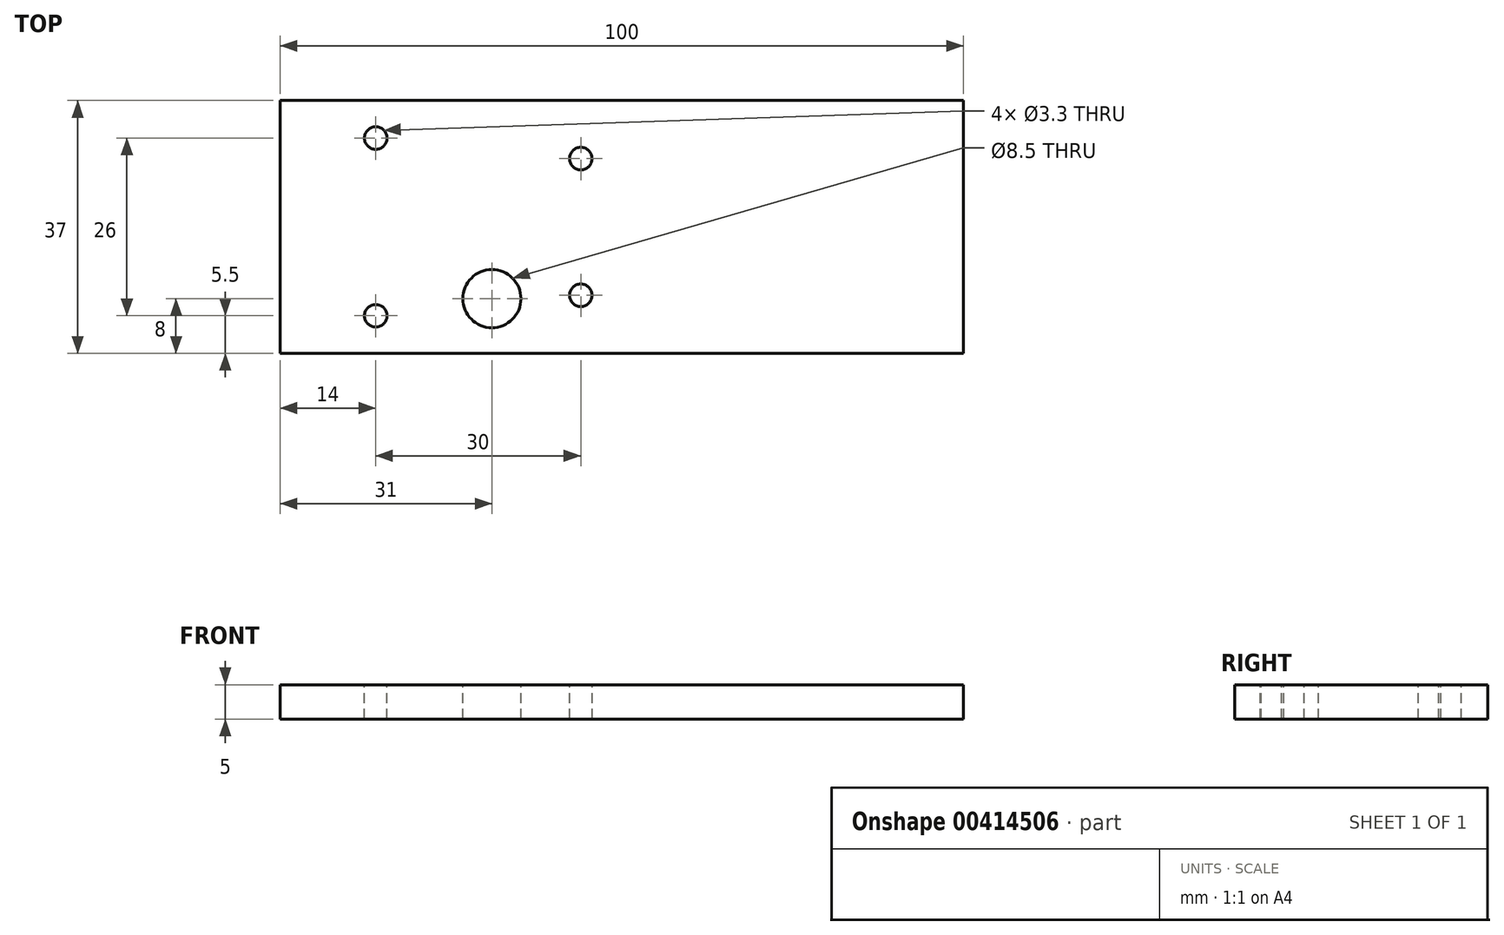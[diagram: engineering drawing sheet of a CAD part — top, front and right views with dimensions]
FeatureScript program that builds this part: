
annotation { "Feature Type Name" : "Feature", "Feature Type Description" : "" }
export const myFeature = defineFeature(function(context is Context, id is Id, definition is map)
    precondition{}
    {
        {
            var Q0;
            Q0=qCreatedBy(makeId("Top.planeOp"),FACE);
            var sketch = newSketch(context, id + "F0", { "sketchPlane" : qUnion([Q0])});
            skLineSegment(sketch, "E0.bottom", {"start": v(-50, 18.5) * mm, "end": v(50, 18.5) * mm});
            skLineSegment(sketch, "E0.top", {"start": v(-50, -18.5) * mm, "end": v(50, -18.5) * mm});
            skLineSegment(sketch, "E0.left", {"start": v(-50, 18.5) * mm, "end": v(-50, -18.5) * mm});
            skLineSegment(sketch, "E0.right", {"start": v(50, 18.5) * mm, "end": v(50, -18.5) * mm});
            skPoint(sketch, "E0.middle", {"position": v(0, 0) * mm});
            skSolve(sketch);
        }
        {
            var Q0;
            Q0 = qSketchRegion(id + "F0", true);
            extrude(context, id + "F1", {"entities" : qUnion([Q0]), "depth" : 5 * mm});
        }
        {
            var Q0;
            Q0=makeQuery(id+"F1.opExtrude","CAP_FACE",FACE,{"disambiguationData":[OSD([sQuery(id+"F0.wireOp",EDGE,"E0.bottom"),sQuery(id+"F0.wireOp",EDGE,"E0.top"),sQuery(id+"F0.wireOp",EDGE,"E0.left"),sQuery(id+"F0.wireOp",EDGE,"E0.right")])],"isStart":false});
            var sketch = newSketch(context, id + "F2", { "sketchPlane" : qUnion([Q0])});
            skLineSegment(sketch, "E1", {"start": v(-36, 13) * mm, "end": v(-36, -13) * mm, "construction": true});
            skPoint(sketch, "E2", {"position": v(-36, 13) * mm});
            skPoint(sketch, "E3", {"position": v(-36, -13) * mm});
            skSolve(sketch);
        }
        {
            var Q0;
            Q0=sQuery(id+"F2.wireOp",VERTEX,"E2");
            var Q1;
            Q1=sQuery(id+"F2.wireOp",VERTEX,"E3");
            var Q2;
            Q2=makeQuery(id+"F1.opExtrude","SWEPT_BODY",BODY,{"disambiguationData":[OSD([sQuery(id+"F0.wireOp",EDGE,"E0.bottom"),sQuery(id+"F0.wireOp",EDGE,"E0.top"),sQuery(id+"F0.wireOp",EDGE,"E0.left"),sQuery(id+"F0.wireOp",EDGE,"E0.right")])]});
            hole(context, id + "F3", {"style" : HoleStyle.SIMPLE, "endStyle" : HoleEndStyle.THROUGH, "standardTappedOrClearance" : lookupTablePath({ "standard" : "ISO", "engagement" : "75%", "pitch" : "0.7 mm", "size" : "M4", "type" : "Tapped" }), "standardBlindInLast" : lookupTablePath({ "standard" : "ISO", "engagement" : "75%", "pitch" : "0.7 mm", "size" : "M4", "type" : "Tapped" }), "holeDiameter" : 3.3 * mm, "showTappedDepth" : true, "tappedDepth" : 5 * mm, "tapClearance" : 2, "startFromSketch" : true, "locations" : qUnion([Q0, Q1]), "scope" : qUnion([Q2]), "majorDiameter" : 4 * mm});
        }
        {
            var Q0;
            Q0=makeQuery(id+"F1.opExtrude","CAP_FACE",FACE,{"disambiguationData":[OSD([sQuery(id+"F0.wireOp",EDGE,"E0.bottom"),sQuery(id+"F0.wireOp",EDGE,"E0.top"),sQuery(id+"F0.wireOp",EDGE,"E0.left"),sQuery(id+"F0.wireOp",EDGE,"E0.right")])],"isStart":false});
            var sketch = newSketch(context, id + "F4", { "sketchPlane" : qUnion([Q0])});
            skPoint(sketch, "E4", {"position": v(-19, -10.5) * mm});
            skSolve(sketch);
        }
        {
            var Q0;
            Q0=sQuery(id+"F4.wireOp",VERTEX,"E4");
            var Q1;
            Q1=makeQuery(id+"F1.opExtrude","SWEPT_BODY",BODY,{"disambiguationData":[OSD([sQuery(id+"F0.wireOp",EDGE,"E0.bottom"),sQuery(id+"F0.wireOp",EDGE,"E0.top"),sQuery(id+"F0.wireOp",EDGE,"E0.left"),sQuery(id+"F0.wireOp",EDGE,"E0.right")])]});
            hole(context, id + "F5", {"style" : HoleStyle.SIMPLE, "endStyle" : HoleEndStyle.THROUGH, "standardTappedOrClearance" : lookupTablePath({ "standard" : "ISO", "engagement" : "75%", "pitch" : "1.5 mm", "size" : "M10", "type" : "Tapped" }), "standardBlindInLast" : lookupTablePath({ "standard" : "ISO", "engagement" : "75%", "pitch" : "1.5 mm", "size" : "M10", "type" : "Tapped" }), "holeDiameter" : 8.5 * mm, "showTappedDepth" : true, "tappedDepth" : 5 * mm, "tapClearance" : 2, "startFromSketch" : true, "locations" : qUnion([Q0]), "scope" : qUnion([Q1]), "majorDiameter" : 10 * mm});
        }
        {
            var Q0;
            Q0=makeQuery(id+"F1.opExtrude","CAP_FACE",FACE,{"disambiguationData":[OSD([sQuery(id+"F0.wireOp",EDGE,"E0.bottom"),sQuery(id+"F0.wireOp",EDGE,"E0.top"),sQuery(id+"F0.wireOp",EDGE,"E0.left"),sQuery(id+"F0.wireOp",EDGE,"E0.right")])],"isStart":false});
            var sketch = newSketch(context, id + "F6", { "sketchPlane" : qUnion([Q0])});
            skLineSegment(sketch, "E5", {"start": v(-6, 10) * mm, "end": v(-6, -10) * mm, "construction": true});
            skPoint(sketch, "E6", {"position": v(-6, 10) * mm});
            skPoint(sketch, "E7", {"position": v(-6, -10) * mm});
            skSolve(sketch);
        }
        {
            var Q0;
            Q0=sQuery(id+"F6.wireOp",VERTEX,"E6");
            var Q1;
            Q1=sQuery(id+"F6.wireOp",VERTEX,"E7");
            var Q2;
            Q2=makeQuery(id+"F1.opExtrude","SWEPT_BODY",BODY,{"disambiguationData":[OSD([sQuery(id+"F0.wireOp",EDGE,"E0.bottom"),sQuery(id+"F0.wireOp",EDGE,"E0.top"),sQuery(id+"F0.wireOp",EDGE,"E0.left"),sQuery(id+"F0.wireOp",EDGE,"E0.right")])]});
            hole(context, id + "F7", {"style" : HoleStyle.SIMPLE, "endStyle" : HoleEndStyle.BLIND, "standardTappedOrClearance" : lookupTablePath({ "standard" : "ISO", "fit" : "Normal", "size" : "M3", "type" : "Clearance" }), "standardBlindInLast" : lookupTablePath({ "fit" : "Standard", "standard" : "ISO", "size" : "M3", "type" : "Clearance" }), "holeDiameter" : 3.3 * mm, "holeDepth" : 6 * mm, "tappedDepth" : 5 * mm, "tapClearance" : 2, "startFromSketch" : true, "locations" : qUnion([Q0, Q1]), "scope" : qUnion([Q2])});
        }
    });
